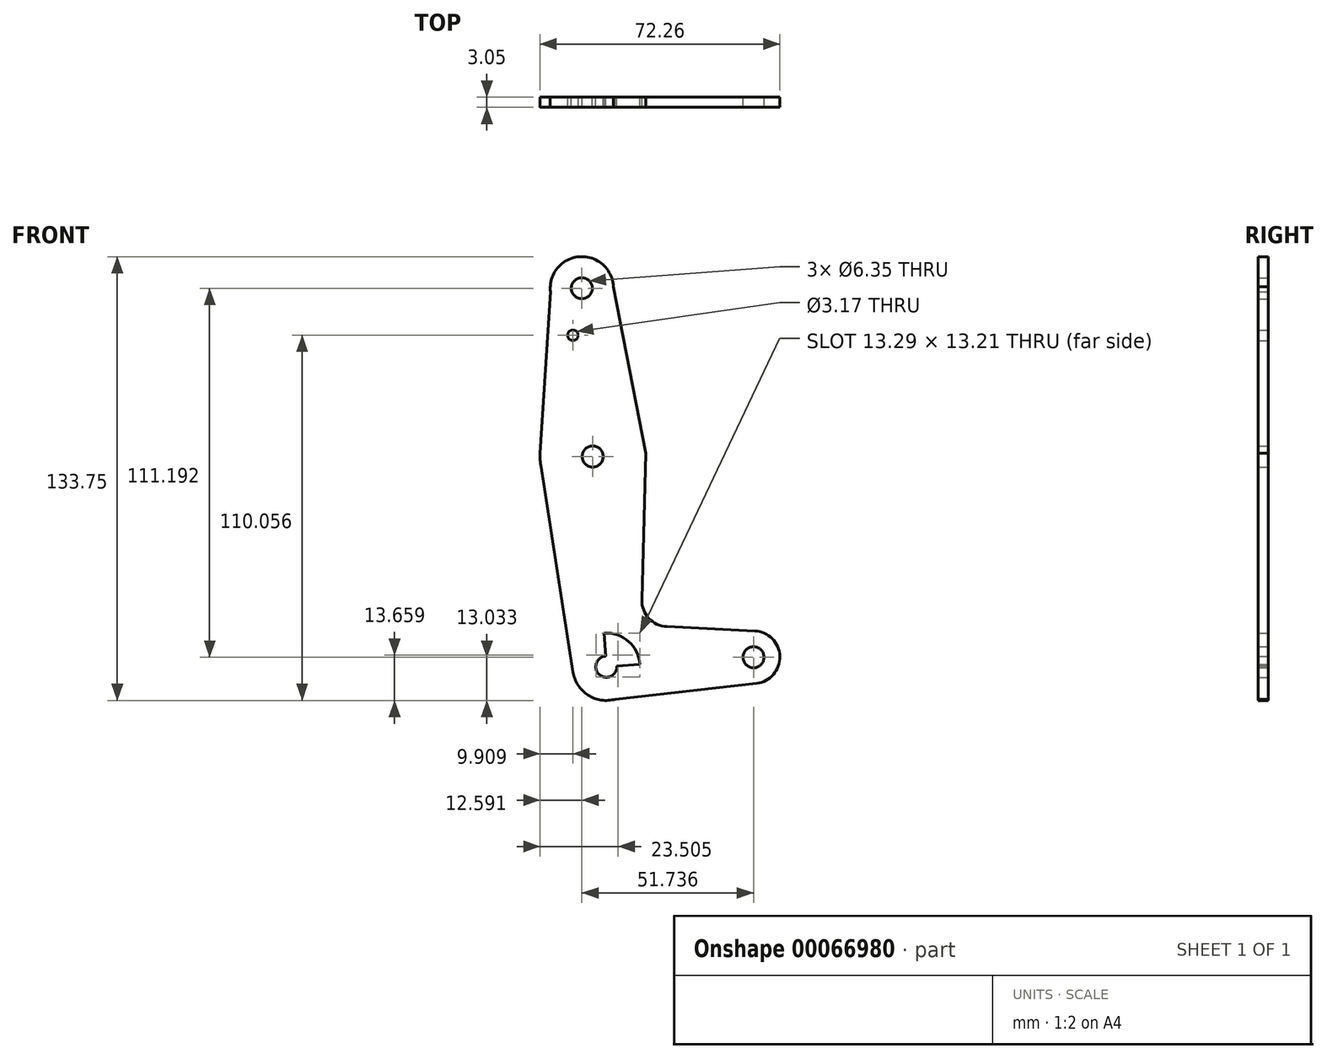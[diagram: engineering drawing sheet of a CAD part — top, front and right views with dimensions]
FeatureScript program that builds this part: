
annotation { "Feature Type Name" : "Feature", "Feature Type Description" : "" }
export const myFeature = defineFeature(function(context is Context, id is Id, definition is map)
    precondition{}
    {
        {
            var Q0;
            Q0=qCreatedBy(makeId("Front.planeOp"),FACE);
            var sketch = newSketch(context, id + "F0", { "sketchPlane" : qUnion([Q0])});
            skLineSegment(sketch, "E0", {"start": v(-41.04, 64.69) * mm, "end": v(-33.66, -49.38) * mm});
            skLineSegment(sketch, "E1", {"start": v(-33.66, -49.38) * mm, "end": v(10.7, -46.5) * mm});
            skLineSegment(sketch, "E2", {"start": v(-37.76, 14) * mm, "end": v(-33.66, -49.38) * mm});
            skCircle(sketch, "E3", {"center": v(-41.04, 64.69) * mm, "radius": 9.53 * mm});
            skCircle(sketch, "E4", {"center": v(-37.76, 14) * mm, "radius": 15.88 * mm});
            skCircle(sketch, "E5", {"center": v(-33.66, -49.38) * mm, "radius": 10.16 * mm});
            skCircle(sketch, "E6", {"center": v(10.7, -46.5) * mm, "radius": 7.94 * mm});
            skLineSegment(sketch, "E7", {"start": v(-50.5, 63.62) * mm, "end": v(-53.6, 15) * mm});
            skLineSegment(sketch, "E8", {"start": v(-31.52, 65.12) * mm, "end": v(-21.78, 15) * mm});
            skLineSegment(sketch, "E9", {"start": v(-53.42, 11.4) * mm, "end": v(-43.7, -50.94) * mm});
            skLineSegment(sketch, "E10", {"start": v(-21.78, 15) * mm, "end": v(-22.96, -29.14) * mm});
            skLineSegment(sketch, "E11", {"start": v(-15.4, -37.3) * mm, "end": v(11.08, -38.58) * mm});
            skLineSegment(sketch, "E12", {"start": v(-34.18, -59.52) * mm, "end": v(11.58, -54.4) * mm});
            skCircle(sketch, "E13", {"center": v(-41.04, 64.69) * mm, "radius": 3.18 * mm});
            skCircle(sketch, "E14", {"center": v(-37.76, 14) * mm, "radius": 3.18 * mm});
            skCircle(sketch, "E15", {"center": v(-33.66, -49.38) * mm, "radius": 3.18 * mm});
            skCircle(sketch, "E16", {"center": v(10.7, -46.5) * mm, "radius": 3.18 * mm});
            skArc(sketch, "E17.filletArc", {"start": v(-22.96, -29.14) * mm, "mid": v(-20.84, -34.76) * mm, "end": v(-15.4, -37.3) * mm});
            skCircle(sketch, "E18", {"center": v(-43.72, 50.52) * mm, "radius": 1.59 * mm});
            skSolve(sketch);
        }
        {
            var Q0;
            Q0 = qSketchRegion(id + "F0", true);
            extrude(context, id + "F1", {"entities" : qUnion([Q0]), "depth" : 3.05 * mm});
        }
    });
